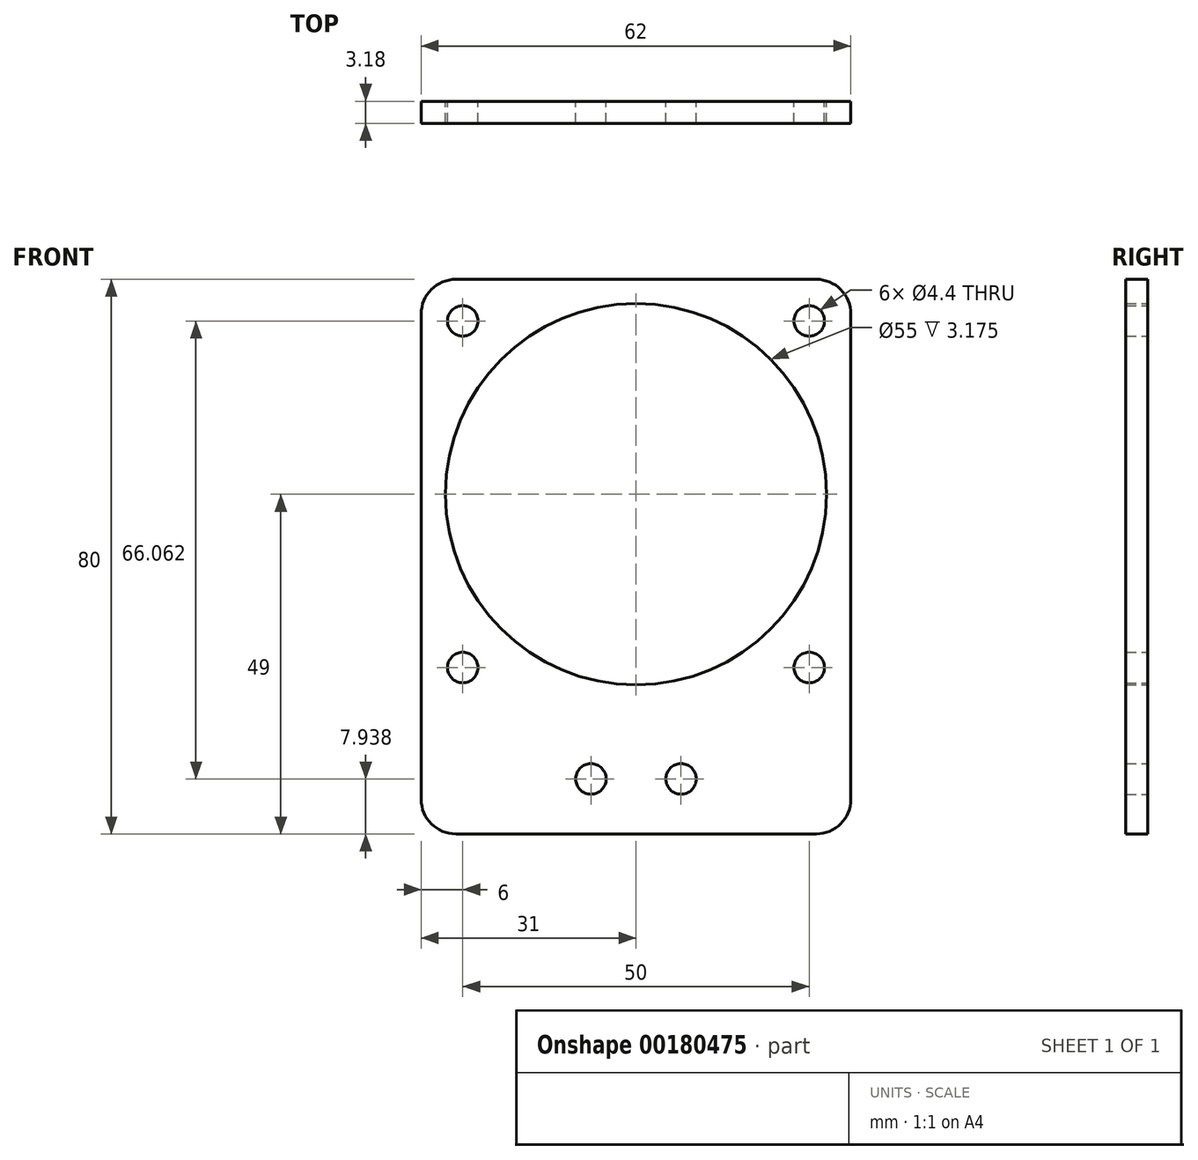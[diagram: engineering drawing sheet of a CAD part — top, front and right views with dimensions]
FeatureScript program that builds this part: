
annotation { "Feature Type Name" : "Feature", "Feature Type Description" : "" }
export const myFeature = defineFeature(function(context is Context, id is Id, definition is map)
    precondition{}
    {
        {
            var Q0;
            Q0=qCreatedBy(makeId("Top.planeOp"),FACE);
            var sketch = newSketch(context, id + "F0", { "sketchPlane" : qUnion([Q0])});
            skLineSegment(sketch, "E0.bottom", {"start": v(31, -1.59) * mm, "end": v(-31, -1.59) * mm});
            skLineSegment(sketch, "E0.top", {"start": v(31, 1.59) * mm, "end": v(-31, 1.59) * mm});
            skLineSegment(sketch, "E0.left", {"start": v(31, -1.59) * mm, "end": v(31, 1.59) * mm});
            skLineSegment(sketch, "E0.right", {"start": v(-31, -1.59) * mm, "end": v(-31, 1.59) * mm});
            skPoint(sketch, "E0.middle", {"position": v(0, 0) * mm});
            skSolve(sketch);
        }
        {
            var Q0;
            Q0 = qSketchRegion(id + "F0", true);
            extrude(context, id + "F1", {"entities" : qUnion([Q0]), "depth" : 80 * mm});
        }
        {
            var Q0;
            Q0=makeQuery(id+"F1.opExtrude","SWEPT_FACE",FACE,{"disambiguationData":[OSD([sQuery(id+"F0.wireOp",EDGE,"E0.top")])]});
            var sketch = newSketch(context, id + "F2", { "sketchPlane" : qUnion([Q0])});
            skPoint(sketch, "E1", {"position": v(-6.5, 7.94) * mm});
            skPoint(sketch, "E2", {"position": v(6.5, 7.94) * mm});
            skSolve(sketch);
        }
        {
            var Q0;
            Q0=sQuery(id+"F2.wireOp",VERTEX,"E1");
            var Q1;
            Q1=sQuery(id+"F2.wireOp",VERTEX,"E2");
            var Q2;
            Q2=makeQuery(id+"F1.opExtrude","SWEPT_BODY",BODY,{"disambiguationData":[OSD([sQuery(id+"F0.wireOp",EDGE,"E0.bottom"),sQuery(id+"F0.wireOp",EDGE,"E0.top"),sQuery(id+"F0.wireOp",EDGE,"E0.left"),sQuery(id+"F0.wireOp",EDGE,"E0.right")])]});
            hole(context, id + "F3", {"style" : HoleStyle.SIMPLE, "endStyle" : HoleEndStyle.THROUGH, "standardTappedOrClearance" : lookupTablePath({ "standard" : "ISO", "fit" : "Normal", "size" : "M4", "type" : "Clearance" }), "standardBlindInLast" : lookupTablePath({ "fit" : "Standard", "standard" : "ISO", "size" : "M4", "type" : "Clearance" }), "holeDiameter" : 4.4 * mm, "locations" : qUnion([Q0, Q1]), "scope" : qUnion([Q2]), "isTappedThrough" : true});
        }
        {
            var Q0;
            Q0=makeQuery(id+"F1.opExtrude","SWEPT_FACE",FACE,{"disambiguationData":[OSD([sQuery(id+"F0.wireOp",EDGE,"E0.top")])]});
            var sketch = newSketch(context, id + "F4", { "sketchPlane" : qUnion([Q0])});
            skCircle(sketch, "E3", {"center": v(0, 49) * mm, "radius": 27.5 * mm});
            skLineSegment(sketch, "E4.bottom", {"start": v(25, 24) * mm, "end": v(-25, 24) * mm, "construction": true});
            skLineSegment(sketch, "E4.top", {"start": v(25, 74) * mm, "end": v(-25, 74) * mm, "construction": true});
            skLineSegment(sketch, "E4.left", {"start": v(25, 24) * mm, "end": v(25, 74) * mm, "construction": true});
            skLineSegment(sketch, "E4.right", {"start": v(-25, 24) * mm, "end": v(-25, 74) * mm, "construction": true});
            skSolve(sketch);
        }
        {
            var Q0;
            Q0=sQuery(id+"F4.wireOp",VERTEX,"E4.right.end");
            var Q1;
            Q1=sQuery(id+"F4.wireOp",VERTEX,"E4.left.end");
            var Q2;
            Q2=sQuery(id+"F4.wireOp",VERTEX,"E4.bottom.start");
            var Q3;
            Q3=sQuery(id+"F4.wireOp",VERTEX,"E4.right.start");
            var Q4;
            Q4=makeQuery(id+"F1.opExtrude","SWEPT_BODY",BODY,{"disambiguationData":[OSD([sQuery(id+"F0.wireOp",EDGE,"E0.bottom"),sQuery(id+"F0.wireOp",EDGE,"E0.top"),sQuery(id+"F0.wireOp",EDGE,"E0.left"),sQuery(id+"F0.wireOp",EDGE,"E0.right")])]});
            hole(context, id + "F5", {"style" : HoleStyle.SIMPLE, "endStyle" : HoleEndStyle.THROUGH, "standardTappedOrClearance" : lookupTablePath({ "standard" : "ISO", "fit" : "Normal", "size" : "M4", "type" : "Clearance" }), "standardBlindInLast" : lookupTablePath({ "fit" : "Standard", "standard" : "ISO", "size" : "M4", "type" : "Clearance" }), "holeDiameter" : 4.4 * mm, "locations" : qUnion([Q0, Q1, Q2, Q3]), "scope" : qUnion([Q4]), "isTappedThrough" : true});
        }
        {
            var Q0;
            Q0 = qSketchRegion(id + "F4", true);
            extrude(context, id + "F6", {"entities" : qUnion([Q0]), "operationType" : NewBodyOperationType.REMOVE, "oppositeDirection" : true, "depth" : 25 * mm});
        }
        {
            var Q0;
            Q0=makeQuery(id+"F1.opExtrude","CAP_EDGE",EDGE,{"disambiguationData":[OSD([sQuery(id+"F0.wireOp",EDGE,"E0.left")])],"isStart":false});
            var Q1;
            Q1=makeQuery(id+"F1.opExtrude","CAP_EDGE",EDGE,{"disambiguationData":[OSD([sQuery(id+"F0.wireOp",EDGE,"E0.right")])],"isStart":false});
            var Q2;
            Q2=makeQuery(id+"F1.opExtrude","CAP_EDGE",EDGE,{"disambiguationData":[OSD([sQuery(id+"F0.wireOp",EDGE,"E0.right")])],"isStart":true});
            var Q3;
            Q3=makeQuery(id+"F1.opExtrude","CAP_EDGE",EDGE,{"disambiguationData":[OSD([sQuery(id+"F0.wireOp",EDGE,"E0.left")])],"isStart":true});
            fillet(context, id + "F7", {"entities" : qUnion([Q0, Q1, Q2, Q3]), "radius" : 5 * mm, "tangentPropagation" : true, "allowEdgeOverflow" : false});
        }
    });
